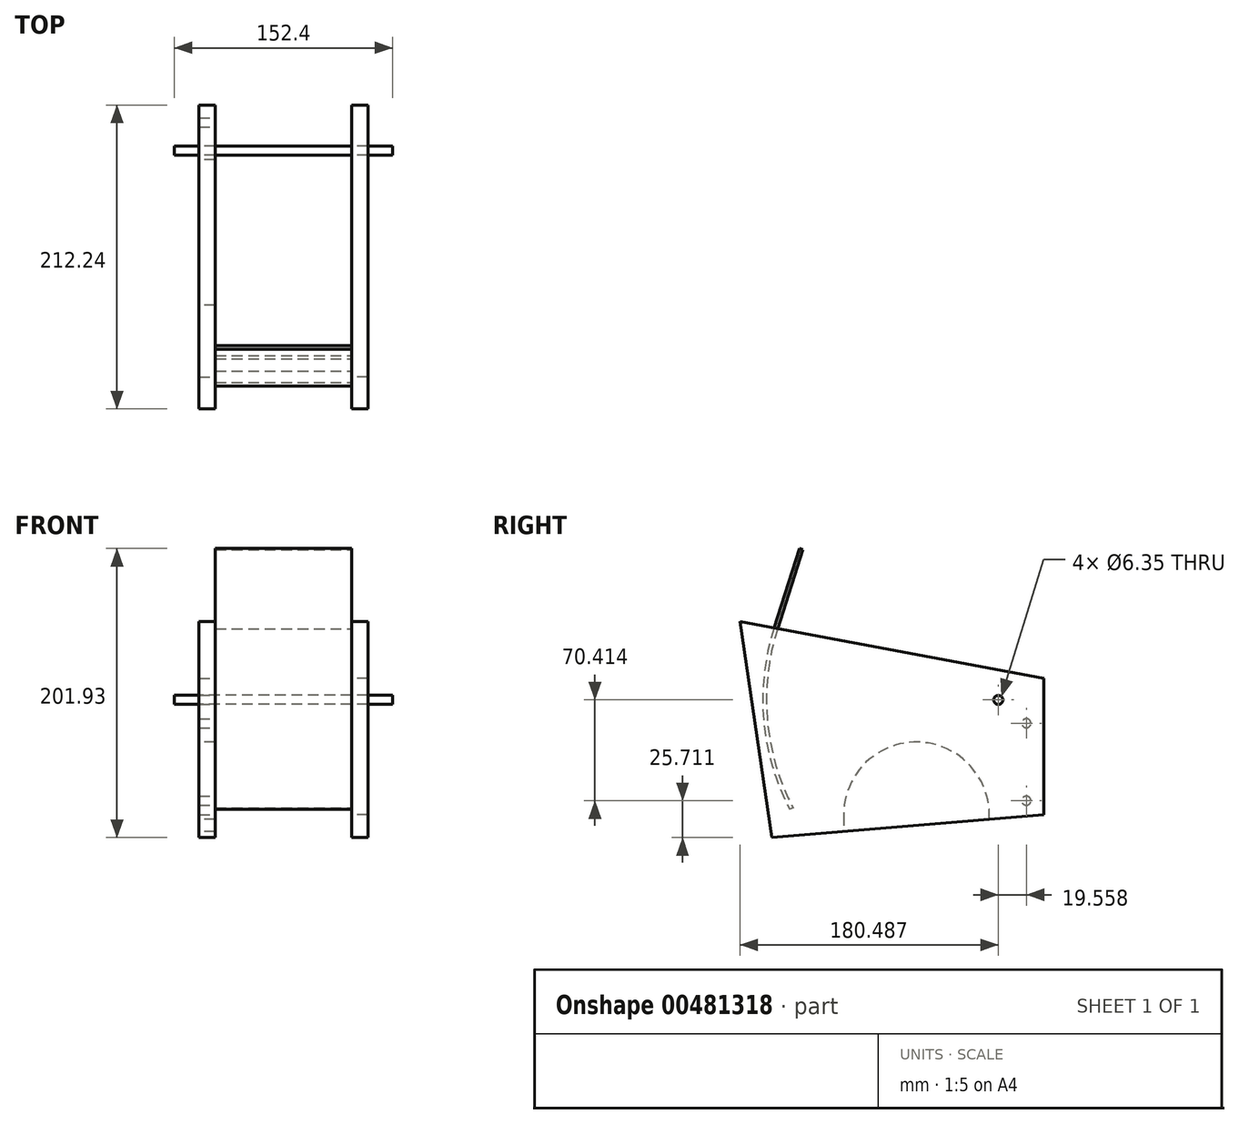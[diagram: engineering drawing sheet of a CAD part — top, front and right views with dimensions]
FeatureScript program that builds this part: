
annotation { "Feature Type Name" : "Feature", "Feature Type Description" : "" }
export const myFeature = defineFeature(function(context is Context, id is Id, definition is map)
    precondition{}
    {
        {
            var Q0;
            Q0=qCreatedBy(makeId("Right.planeOp"),FACE);
            var sketch = newSketch(context, id + "F0", { "sketchPlane" : qUnion([Q0])});
            skLineSegment(sketch, "E0", {"start": v(122.12, 51.37) * mm, "end": v(-90.12, 90.98) * mm});
            skLineSegment(sketch, "E1", {"start": v(-90.12, 90.98) * mm, "end": v(-67.72, -59.76) * mm});
            skLineSegment(sketch, "E2", {"start": v(122.12, 51.37) * mm, "end": v(122.12, -43.88) * mm});
            skLineSegment(sketch, "E3", {"start": v(-67.72, -59.76) * mm, "end": v(122.12, -43.88) * mm});
            skCircle(sketch, "E4", {"center": v(90.37, 36.36) * mm, "radius": 3.18 * mm});
            skCircle(sketch, "E5", {"center": v(109.92, 20.05) * mm, "radius": 3.18 * mm});
            skCircle(sketch, "E6", {"center": v(109.92, -34.05) * mm, "radius": 3.18 * mm});
            skSolve(sketch);
        }
        {
            var Q0;
            Q0 = qSketchRegion(id + "F0", true);
            var Q1;
            Q1=makeQuery(id+"F0.imprint","IMPRINT",FACE,{"disambiguationData":[TD([[makeQuery(id+"F0.imprint","IMPRINT",EDGE,{"derivedFrom":sQuery(id+"F0.wireOp",EDGE,"E4")}),1.0]])]});
            var Q2;
            Q2=makeQuery(id+"F0.imprint","IMPRINT",FACE,{"disambiguationData":[TD([[makeQuery(id+"F0.imprint","IMPRINT",EDGE,{"derivedFrom":sQuery(id+"F0.wireOp",EDGE,"E5")}),1.0]])]});
            var Q3;
            Q3=makeQuery(id+"F0.imprint","IMPRINT",FACE,{"disambiguationData":[TD([[makeQuery(id+"F0.imprint","IMPRINT",EDGE,{"derivedFrom":sQuery(id+"F0.wireOp",EDGE,"E6")}),1.0]])]});
            extrude(context, id + "F1", {"entities" : qUnion([Q0, Q1, Q2, Q3]), "depth" : 11.43 * mm});
        }
        {
            var Q0;
            Q0=makeQuery(id+"F1.opExtrude","SWEPT_BODY",BODY,{"disambiguationData":[OSD([sQuery(id+"F0.wireOp",EDGE,"E0"),sQuery(id+"F0.wireOp",EDGE,"E1"),sQuery(id+"F0.wireOp",EDGE,"E2"),sQuery(id+"F0.wireOp",EDGE,"E3"),sQuery(id+"F0.wireOp",EDGE,"E4"),sQuery(id+"F0.wireOp",EDGE,"E5"),sQuery(id+"F0.wireOp",EDGE,"E6")])]});
            transform(context, id + "F2", {"entities" : qUnion([Q0]), "transformType" : TransformType.TRANSLATION_3D, "dx" : 47.62 * mm, "dy" : 0 * mm, "dz" : 0 * mm, "makeCopy" : false});
        }
        {
            var Q0;
            Q0=makeQuery(id+"F1.opExtrude","SWEPT_BODY",BODY,{"disambiguationData":[OSD([sQuery(id+"F0.wireOp",EDGE,"E0"),sQuery(id+"F0.wireOp",EDGE,"E1"),sQuery(id+"F0.wireOp",EDGE,"E2"),sQuery(id+"F0.wireOp",EDGE,"E3"),sQuery(id+"F0.wireOp",EDGE,"E4"),sQuery(id+"F0.wireOp",EDGE,"E5"),sQuery(id+"F0.wireOp",EDGE,"E6")])]});
            var Q1;
            Q1=qCreatedBy(makeId("Right.planeOp"),FACE);
            mirror(context, id + "F3", {"entities" : qUnion([Q0]), "mirrorPlane" : qUnion([Q1])});
        }
        {
            var Q0;
            Q0=makeQuery(id+"F3.opPattern","COPY",FACE,{"derivedFrom":makeQuery(id+"F1.opExtrude","CAP_FACE",FACE,{"disambiguationData":[OSD([sQuery(id+"F0.wireOp",EDGE,"E0"),sQuery(id+"F0.wireOp",EDGE,"E1"),sQuery(id+"F0.wireOp",EDGE,"E2"),sQuery(id+"F0.wireOp",EDGE,"E3"),sQuery(id+"F0.wireOp",EDGE,"E4"),sQuery(id+"F0.wireOp",EDGE,"E5"),sQuery(id+"F0.wireOp",EDGE,"E6")])],"isStart":false}),"instanceName":"1"});
            var sketch = newSketch(context, id + "F4", { "sketchPlane" : qUnion([Q0])});
            skLineSegment(sketch, "E7", {"start": v(-122.12, -43.88) * mm, "end": v(-33.22, -43.88) * mm});
            skCircle(sketch, "E8", {"center": v(-33.22, -43.88) * mm, "radius": 50.8 * mm});
            skLineSegment(sketch, "E9", {"start": v(17.58, -43.88) * mm, "end": v(17.58, -55.57) * mm});
            skSolve(sketch);
        }
        {
            var Q0;
            {var subQ0=sQuery(id+"F4.wireOp",EDGE,"E8");var subQ1=makeQuery(id+"F4.imprint","INTERSECT",VERTEX,{"derivedFrom":[subQ0,sQuery(id+"F4.wireOp",EDGE,"E9")]});Q0=makeQuery(id+"F4.imprint","IMPRINT",FACE,{"disambiguationData":[TD([[makeQuery(id+"F4.imprint","IMPRINT",EDGE,{"disambiguationData":[TD([[subQ1,-1.0]])],"derivedFrom":subQ0}),1.0]])]});}
            var Q1;
            {var subQ0=sQuery(id+"F4.wireOp",EDGE,"E9");Q1=makeQuery(id+"F4.imprint","IMPRINT",FACE,{"disambiguationData":[TD([[makeQuery(id+"F4.imprint","IMPRINT",EDGE,{"derivedFrom":subQ0}),-1.0]])]});}
            extrude(context, id + "F5", {"entities" : qUnion([Q0, Q1]), "operationType" : NewBodyOperationType.REMOVE, "oppositeDirection" : true, "depth" : 25.4 * mm});
        }
        {
            var Q0;
            Q0=sQuery(id+"F0.wireOp",VERTEX,"E4.center");
            var Q1;
            Q1=makeQuery(id+"F3.opPattern","COPY",BODY,{"derivedFrom":makeQuery(id+"F1.opExtrude","SWEPT_BODY",BODY,{"disambiguationData":[OSD([sQuery(id+"F0.wireOp",EDGE,"E0"),sQuery(id+"F0.wireOp",EDGE,"E1"),sQuery(id+"F0.wireOp",EDGE,"E2"),sQuery(id+"F0.wireOp",EDGE,"E3")])]}),"instanceName":"1"});
            hole(context, id + "F6", {"style" : HoleStyle.SIMPLE, "endStyle" : HoleEndStyle.BLIND, "holeDiameter" : 6.35 * mm, "holeDepth" : 76.2 * mm, "isTappedThrough" : true, "tappedDepth" : 12.7 * mm, "tapClearance" : 3, "startFromSketch" : true, "locations" : qUnion([Q0]), "scope" : qUnion([Q1])});
        }
        {
            var Q0;
            Q0=sQuery(id+"F0.wireOp",VERTEX,"E5.center");
            var Q1;
            Q1=makeQuery(id+"F3.opPattern","COPY",BODY,{"derivedFrom":makeQuery(id+"F1.opExtrude","SWEPT_BODY",BODY,{"disambiguationData":[OSD([sQuery(id+"F0.wireOp",EDGE,"E0"),sQuery(id+"F0.wireOp",EDGE,"E1"),sQuery(id+"F0.wireOp",EDGE,"E2"),sQuery(id+"F0.wireOp",EDGE,"E3")])]}),"instanceName":"1"});
            hole(context, id + "F7", {"style" : HoleStyle.SIMPLE, "endStyle" : HoleEndStyle.BLIND, "holeDiameter" : 6.35 * mm, "holeDepth" : 76.2 * mm, "isTappedThrough" : true, "tappedDepth" : 12.7 * mm, "tapClearance" : 3, "startFromSketch" : true, "locations" : qUnion([Q0]), "scope" : qUnion([Q1])});
        }
        {
            var Q0;
            Q0=sQuery(id+"F0.wireOp",VERTEX,"E6.center");
            var Q1;
            Q1=makeQuery(id+"F3.opPattern","COPY",BODY,{"derivedFrom":makeQuery(id+"F1.opExtrude","SWEPT_BODY",BODY,{"disambiguationData":[OSD([sQuery(id+"F0.wireOp",EDGE,"E0"),sQuery(id+"F0.wireOp",EDGE,"E1"),sQuery(id+"F0.wireOp",EDGE,"E2"),sQuery(id+"F0.wireOp",EDGE,"E3")])]}),"instanceName":"1"});
            hole(context, id + "F8", {"style" : HoleStyle.SIMPLE, "endStyle" : HoleEndStyle.BLIND, "holeDiameter" : 6.35 * mm, "holeDepth" : 76.2 * mm, "isTappedThrough" : true, "tappedDepth" : 12.7 * mm, "tapClearance" : 3, "startFromSketch" : true, "locations" : qUnion([Q0]), "scope" : qUnion([Q1])});
        }
        {
            var Q0;
            Q0=sQuery(id+"F0.wireOp",VERTEX,"E4.center");
            var Q1;
            Q1=makeQuery(id+"F1.opExtrude","SWEPT_BODY",BODY,{"disambiguationData":[OSD([sQuery(id+"F0.wireOp",EDGE,"E0"),sQuery(id+"F0.wireOp",EDGE,"E1"),sQuery(id+"F0.wireOp",EDGE,"E2"),sQuery(id+"F0.wireOp",EDGE,"E3")])]});
            hole(context, id + "F9", {"style" : HoleStyle.SIMPLE, "endStyle" : HoleEndStyle.BLIND, "oppositeDirection" : true, "holeDiameter" : 6.35 * mm, "holeDepth" : 76.2 * mm, "isTappedThrough" : true, "tappedDepth" : 12.7 * mm, "tapClearance" : 3, "startFromSketch" : true, "locations" : qUnion([Q0]), "scope" : qUnion([Q1])});
        }
        {
            var Q0;
            Q0=makeQuery(id+"F1.opExtrude","CAP_FACE",FACE,{"disambiguationData":[OSD([sQuery(id+"F0.wireOp",EDGE,"E0"),sQuery(id+"F0.wireOp",EDGE,"E1"),sQuery(id+"F0.wireOp",EDGE,"E2"),sQuery(id+"F0.wireOp",EDGE,"E3")])],"isStart":true});
            var sketch = newSketch(context, id + "F10", { "sketchPlane" : qUnion([Q0])});
            skCircle(sketch, "E10", {"center": v(-90.37, 36.36) * mm, "radius": 66.68 * mm});
            skCircle(sketch, "E11.0", {"center": v(-90.37, 36.36) * mm, "radius": 161.93 * mm});
            skCircle(sketch, "E12.0", {"center": v(-90.37, 36.36) * mm, "radius": 164.47 * mm});
            skLineSegment(sketch, "E13", {"start": v(52.96, -38.98) * mm, "end": v(55.23, -40.13) * mm});
            skLineSegment(sketch, "E14", {"start": v(66.26, 86.53) * mm, "end": v(48.44, 142.17) * mm});
            skLineSegment(sketch, "E15", {"start": v(48.44, 142.17) * mm, "end": v(46.02, 141.4) * mm});
            skLineSegment(sketch, "E16", {"start": v(46.02, 141.4) * mm, "end": v(63.74, 86.06) * mm});
            skSolve(sketch);
        }
        {
            var Q0;
            {var subQ0=sQuery(id+"F10.wireOp",EDGE,"E14");Q0=makeQuery(id+"F10.imprint","IMPRINT",FACE,{"disambiguationData":[TD([[makeQuery(id+"F10.imprint","IMPRINT",EDGE,{"derivedFrom":subQ0}),1.0]])]});}
            var Q1;
            {var subQ1=makeQuery(id+"F1.opExtrude","CAP_EDGE",EDGE,{"disambiguationData":[OSD([sQuery(id+"F0.wireOp",EDGE,"E0")])],"isStart":true});var subQ3=sQuery(id+"F10.wireOp",EDGE,"E16");var subQ5=makeQuery(id+"F10.imprint","INTERSECT",VERTEX,{"derivedFrom":[subQ1,subQ3]});Q1=makeQuery(id+"F10.imprint","IMPRINT",FACE,{"disambiguationData":[TD([[makeQuery(id+"F10.imprint","IMPRINT",EDGE,{"disambiguationData":[TD([[subQ5,1.0]])],"derivedFrom":subQ3}),1.0]])]});}
            var Q2;
            {var subQ4=sQuery(id+"F10.wireOp",EDGE,"E13");Q2=makeQuery(id+"F10.imprint","IMPRINT",FACE,{"disambiguationData":[TD([[makeQuery(id+"F10.imprint","IMPRINT",EDGE,{"derivedFrom":subQ4}),1.0]])]});}
            extrude(context, id + "F11", {"entities" : qUnion([Q0, Q1, Q2]), "depth" : 95.25 * mm});
        }
        {
            var Q0;
            Q0=makeQuery(id+"F0.imprint","IMPRINT",FACE,{"disambiguationData":[TD([[makeQuery(id+"F0.imprint","IMPRINT",EDGE,{"derivedFrom":sQuery(id+"F0.wireOp",EDGE,"E4")}),1.0]])]});
            extrude(context, id + "F12", {"entities" : qUnion([Q0]), "endBound" : BoundingType.SYMMETRIC, "depth" : 152.4 * mm, "offsetDistance" : 25.4 * mm});
        }
    });
